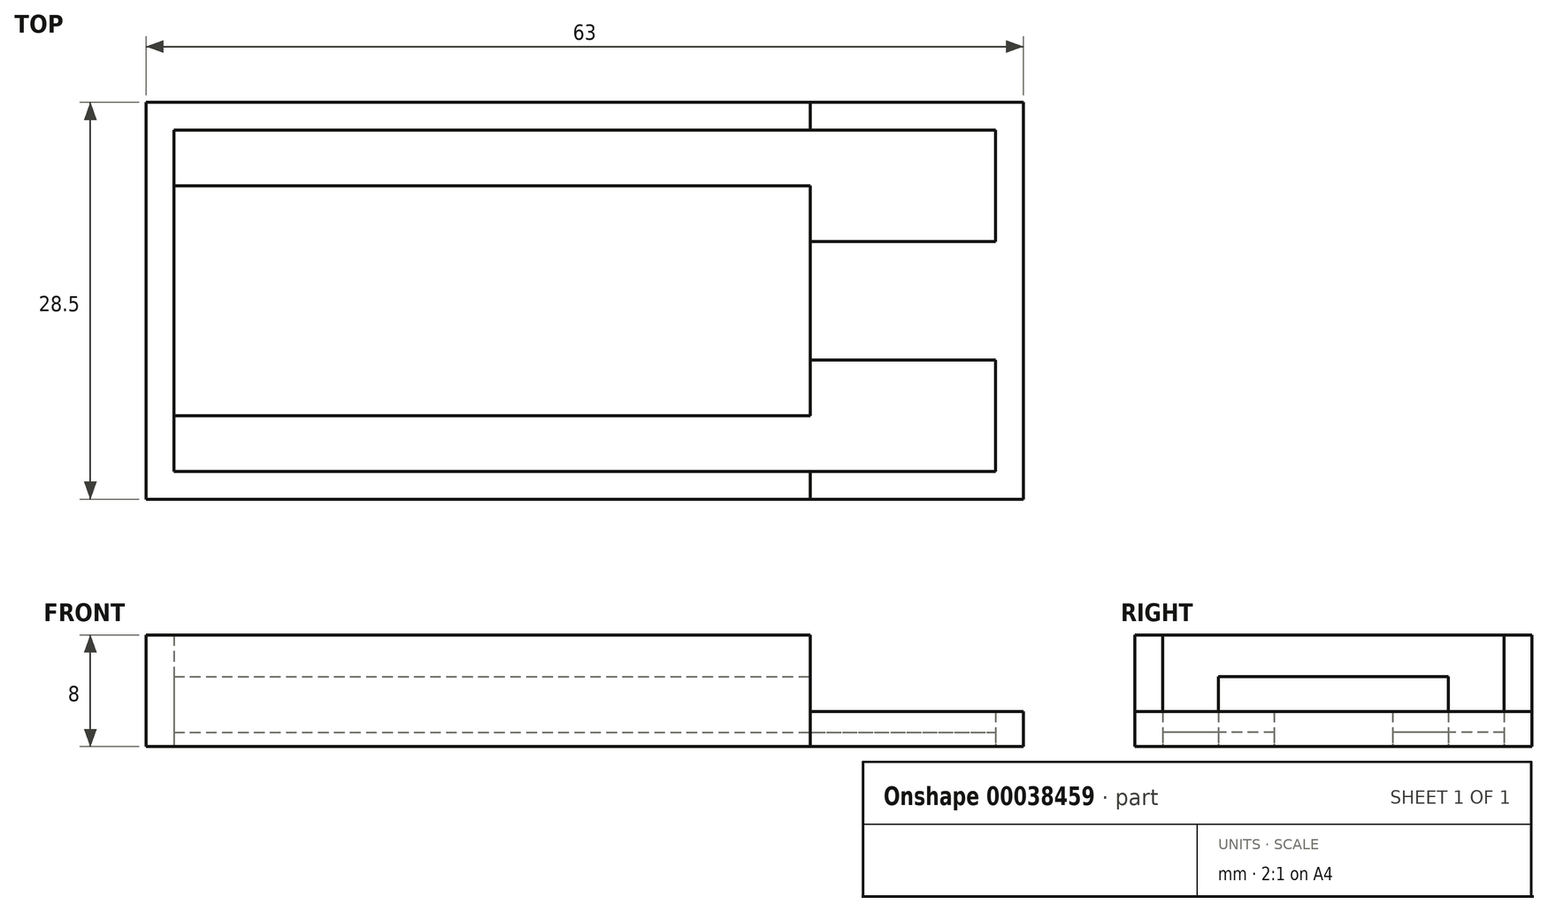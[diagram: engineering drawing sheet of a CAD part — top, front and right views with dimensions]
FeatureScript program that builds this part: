
annotation { "Feature Type Name" : "Feature", "Feature Type Description" : "" }
export const myFeature = defineFeature(function(context is Context, id is Id, definition is map)
    precondition{}
    {
        {
            var Q0;
            Q0=qCreatedBy(makeId("Top.planeOp"),FACE);
            var sketch = newSketch(context, id + "F0", { "sketchPlane" : qUnion([Q0])});
            skLineSegment(sketch, "E0", {"start": v(-83.28, 24.5) * mm, "end": v(93.04, 24.5) * mm, "construction": true});
            skLineSegment(sketch, "E1", {"start": v(59, -21.37) * mm, "end": v(59, 62.02) * mm, "construction": true});
            skLineSegment(sketch, "E2", {"start": v(-82.03, 20.5) * mm, "end": v(90.12, 20.5) * mm, "construction": true});
            skLineSegment(sketch, "E3", {"start": v(-82.58, 4) * mm, "end": v(90.12, 4) * mm, "construction": true});
            skLineSegment(sketch, "E4", {"start": v(45.7, 55.46) * mm, "end": v(45.7, -21.13) * mm, "construction": true});
            skLineSegment(sketch, "E5", {"start": v(-2, 34.22) * mm, "end": v(-2, -12.72) * mm, "construction": true});
            skLineSegment(sketch, "E6", {"start": v(-8.23, 26.5) * mm, "end": v(67.64, 26.5) * mm, "construction": true});
            skLineSegment(sketch, "E7", {"start": v(61, 36.16) * mm, "end": v(61, -15.62) * mm, "construction": true});
            skLineSegment(sketch, "E8", {"start": v(68.06, -2) * mm, "end": v(-8.92, -2) * mm, "construction": true});
            skLineSegment(sketch, "E9", {"start": v(34.9, 16.5) * mm, "end": v(73.13, 16.5) * mm, "construction": true});
            skLineSegment(sketch, "E10", {"start": v(34.68, 8) * mm, "end": v(73.78, 8) * mm, "construction": true});
            skLineSegment(sketch, "E11.bottom", {"start": v(59, 26.5) * mm, "end": v(61, 26.5) * mm});
            skLineSegment(sketch, "E11.top", {"start": v(59, -2) * mm, "end": v(61, -2) * mm});
            skLineSegment(sketch, "E11.left", {"start": v(59, 26.5) * mm, "end": v(59, -2) * mm});
            skLineSegment(sketch, "E11.right", {"start": v(61, 26.5) * mm, "end": v(61, -2) * mm});
            skLineSegment(sketch, "E12.bottom", {"start": v(45.7, 26.5) * mm, "end": v(59, 26.5) * mm});
            skLineSegment(sketch, "E12.top", {"start": v(45.7, 24.5) * mm, "end": v(59, 24.5) * mm});
            skLineSegment(sketch, "E12.left", {"start": v(45.7, 26.5) * mm, "end": v(45.7, 24.5) * mm});
            skLineSegment(sketch, "E12.right", {"start": v(59, 26.5) * mm, "end": v(59, 24.5) * mm});
            skLineSegment(sketch, "E13.top", {"start": v(45.7, 16.5) * mm, "end": v(59, 16.5) * mm});
            skLineSegment(sketch, "E13.left", {"start": v(45.7, 24.5) * mm, "end": v(45.7, 16.5) * mm});
            skLineSegment(sketch, "E13.right", {"start": v(59, 24.5) * mm, "end": v(59, 16.5) * mm});
            skLineSegment(sketch, "E14.top", {"start": v(45.7, 8) * mm, "end": v(59, 8) * mm});
            skLineSegment(sketch, "E14.left", {"start": v(45.7, 16.5) * mm, "end": v(45.7, 8) * mm});
            skLineSegment(sketch, "E14.right", {"start": v(59, 16.5) * mm, "end": v(59, 8) * mm});
            skLineSegment(sketch, "E15.top", {"start": v(45.7, 0) * mm, "end": v(59, 0) * mm});
            skLineSegment(sketch, "E15.left", {"start": v(45.7, 8) * mm, "end": v(45.7, 0) * mm});
            skLineSegment(sketch, "E15.right", {"start": v(59, 8) * mm, "end": v(59, 0) * mm});
            skLineSegment(sketch, "E16.top", {"start": v(45.7, -2) * mm, "end": v(59, -2) * mm});
            skLineSegment(sketch, "E16.left", {"start": v(45.7, 0) * mm, "end": v(45.7, -2) * mm});
            skLineSegment(sketch, "E16.right", {"start": v(59, 0) * mm, "end": v(59, -2) * mm});
            skLineSegment(sketch, "E17.bottom", {"start": v(0, 24.5) * mm, "end": v(45.7, 24.5) * mm});
            skLineSegment(sketch, "E17.top", {"start": v(0, 20.5) * mm, "end": v(45.7, 20.5) * mm});
            skLineSegment(sketch, "E17.left", {"start": v(0, 24.5) * mm, "end": v(0, 20.5) * mm});
            skLineSegment(sketch, "E17.right", {"start": v(45.7, 24.5) * mm, "end": v(45.7, 20.5) * mm});
            skLineSegment(sketch, "E18.top", {"start": v(0, 4) * mm, "end": v(45.7, 4) * mm});
            skLineSegment(sketch, "E18.left", {"start": v(0, 20.5) * mm, "end": v(0, 4) * mm});
            skLineSegment(sketch, "E18.right", {"start": v(45.7, 20.5) * mm, "end": v(45.7, 4) * mm});
            skLineSegment(sketch, "E19.top", {"start": v(0, 0) * mm, "end": v(45.7, 0) * mm});
            skLineSegment(sketch, "E19.left", {"start": v(0, 4) * mm, "end": v(0, 0) * mm});
            skLineSegment(sketch, "E19.right", {"start": v(45.7, 4) * mm, "end": v(45.7, 0) * mm});
            skLineSegment(sketch, "E20", {"start": v(45.7, 26.5) * mm, "end": v(-2, 26.5) * mm});
            skLineSegment(sketch, "E21", {"start": v(-2, 26.5) * mm, "end": v(-2, -2) * mm});
            skLineSegment(sketch, "E22", {"start": v(-2, -2) * mm, "end": v(45.7, -2) * mm});
            skLineSegment(sketch, "E23.bottom", {"start": v(59, 16.5) * mm, "end": v(61, 16.5) * mm});
            skLineSegment(sketch, "E23.top", {"start": v(59, 8) * mm, "end": v(61, 8) * mm});
            skLineSegment(sketch, "E23.right", {"start": v(61, 16.5) * mm, "end": v(61, 8) * mm});
            skSolve(sketch);
        }
        {
            var Q0;
            Q0=makeQuery(id+"F0.imprint","IMPRINT",FACE,{"disambiguationData":[TD([[makeQuery(id+"F0.imprint","IMPRINT",EDGE,{"derivedFrom":sQuery(id+"F0.wireOp",EDGE,"E12.top")}),-1.0]])]});
            var Q1;
            {var subQ1=sQuery(id+"F0.wireOp",EDGE,"E14.top");Q1=makeQuery(id+"F0.imprint","IMPRINT",FACE,{"disambiguationData":[TD([[makeQuery(id+"F0.imprint","IMPRINT",EDGE,{"derivedFrom":subQ1}),-1.0]])]});}
            var Q2;
            Q2=makeQuery(id+"F0.imprint","IMPRINT",FACE,{"disambiguationData":[TD([[makeQuery(id+"F0.imprint","IMPRINT",EDGE,{"derivedFrom":sQuery(id+"F0.wireOp",EDGE,"E17.bottom")}),-1.0]])]});
            var Q3;
            Q3=makeQuery(id+"F0.imprint","IMPRINT",FACE,{"disambiguationData":[TD([[makeQuery(id+"F0.imprint","IMPRINT",EDGE,{"derivedFrom":sQuery(id+"F0.wireOp",EDGE,"E18.top")}),-1.0]])]});
            extrude(context, id + "F1", {"entities" : qUnion([Q0, Q1, Q2, Q3]), "depth" : 1 * mm});
        }
        {
            var Q0;
            Q0=makeQuery(id+"F0.imprint","IMPRINT",FACE,{"disambiguationData":[TD([[makeQuery(id+"F0.imprint","IMPRINT",EDGE,{"derivedFrom":sQuery(id+"F0.wireOp",EDGE,"E12.bottom")}),-1.0]])]});
            var Q1;
            {var subQ0=sQuery(id+"F0.wireOp",EDGE,"E13.top");Q1=makeQuery(id+"F0.imprint","IMPRINT",FACE,{"disambiguationData":[TD([[makeQuery(id+"F0.imprint","IMPRINT",EDGE,{"derivedFrom":subQ0}),-1.0]])]});}
            var Q2;
            Q2=makeQuery(id+"F0.imprint","IMPRINT",FACE,{"disambiguationData":[TD([[makeQuery(id+"F0.imprint","IMPRINT",EDGE,{"derivedFrom":sQuery(id+"F0.wireOp",EDGE,"E15.top")}),-1.0]])]});
            var Q3;
            Q3=makeQuery(id+"F0.imprint","IMPRINT",FACE,{"disambiguationData":[TD([[makeQuery(id+"F0.imprint","IMPRINT",EDGE,{"derivedFrom":sQuery(id+"F0.wireOp",EDGE,"E23.bottom")}),-1.0]])]});
            var Q4;
            {var subQ1=sQuery(id+"F0.wireOp",EDGE,"E11.top");Q4=makeQuery(id+"F0.imprint","IMPRINT",FACE,{"disambiguationData":[TD([[makeQuery(id+"F0.imprint","IMPRINT",EDGE,{"derivedFrom":subQ1}),1.0]])]});}
            var Q5;
            {var subQ2=sQuery(id+"F0.wireOp",EDGE,"E11.bottom");Q5=makeQuery(id+"F0.imprint","IMPRINT",FACE,{"disambiguationData":[TD([[makeQuery(id+"F0.imprint","IMPRINT",EDGE,{"derivedFrom":subQ2}),-1.0]])]});}
            extrude(context, id + "F2", {"entities" : qUnion([Q0, Q1, Q2, Q3, Q4, Q5]), "depth" : 2.5 * mm});
        }
        {
            var Q0;
            {var subQ4=sQuery(id+"F0.wireOp",EDGE,"E17.top");Q0=makeQuery(id+"F0.imprint","IMPRINT",FACE,{"disambiguationData":[TD([[makeQuery(id+"F0.imprint","IMPRINT",EDGE,{"derivedFrom":subQ4}),-1.0]])]});}
            extrude(context, id + "F3", {"entities" : qUnion([Q0]), "depth" : 5 * mm});
        }
        {
            var Q0;
            Q0=makeQuery(id+"F0.imprint","IMPRINT",FACE,{"disambiguationData":[TD([[makeQuery(id+"F0.imprint","IMPRINT",EDGE,{"derivedFrom":sQuery(id+"F0.wireOp",EDGE,"E12.left")}),-1.0]])]});
            extrude(context, id + "F4", {"entities" : qUnion([Q0]), "depth" : 8 * mm});
        }
    });
